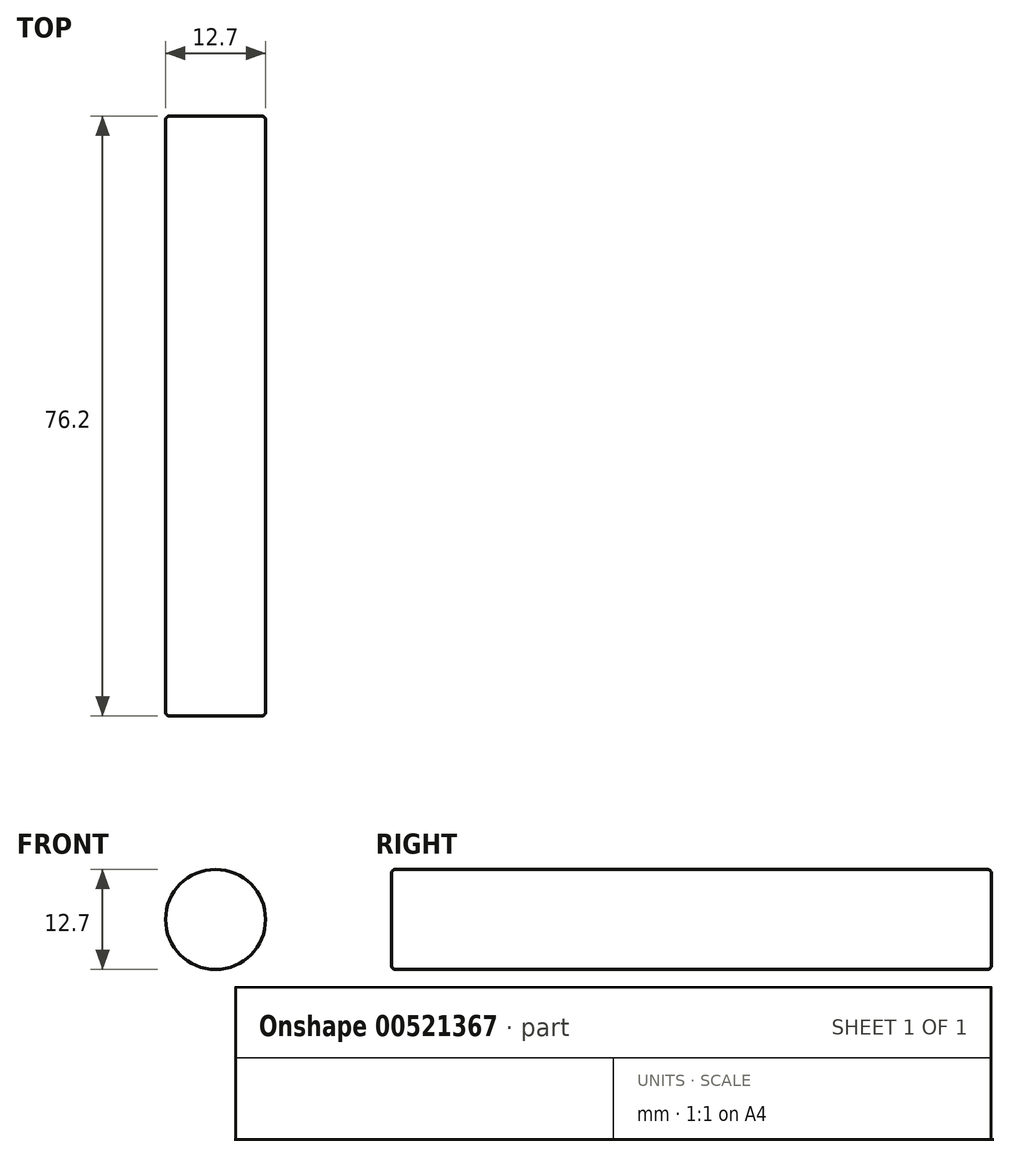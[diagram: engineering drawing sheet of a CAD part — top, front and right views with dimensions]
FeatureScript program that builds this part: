
annotation { "Feature Type Name" : "Feature", "Feature Type Description" : "" }
export const myFeature = defineFeature(function(context is Context, id is Id, definition is map)
    precondition{}
    {
        {
            var Q0;
            Q0=qCreatedBy(makeId("Front.planeOp"),FACE);
            var sketch = newSketch(context, id + "F0", { "sketchPlane" : qUnion([Q0])});
            skCircle(sketch, "E0", {"center": v(0, 0) * mm, "radius": 6.35 * mm});
            skSolve(sketch);
        }
        {
            var Q0;
            Q0 = qSketchRegion(id + "F0", true);
            extrude(context, id + "F1", {"entities" : qUnion([Q0]), "depth" : 76.2 * mm, "offsetDistance" : 25.4 * mm});
        }
        {
            var Q0;
            Q0=makeQuery(id+"F1.opExtrude","CAP_EDGE",EDGE,{"disambiguationData":[OSD([sQuery(id+"F0.wireOp",EDGE,"E0")])],"isStart":false});
            var Q1;
            Q1=makeQuery(id+"F1.opExtrude","CAP_EDGE",EDGE,{"disambiguationData":[OSD([sQuery(id+"F0.wireOp",EDGE,"E0")])],"isStart":true});
            fillet(context, id + "F2", {"entities" : qUnion([Q0, Q1]), "radius" : 0.5 * mm, "tangentPropagation" : true, "allowEdgeOverflow" : false});
        }
    });
